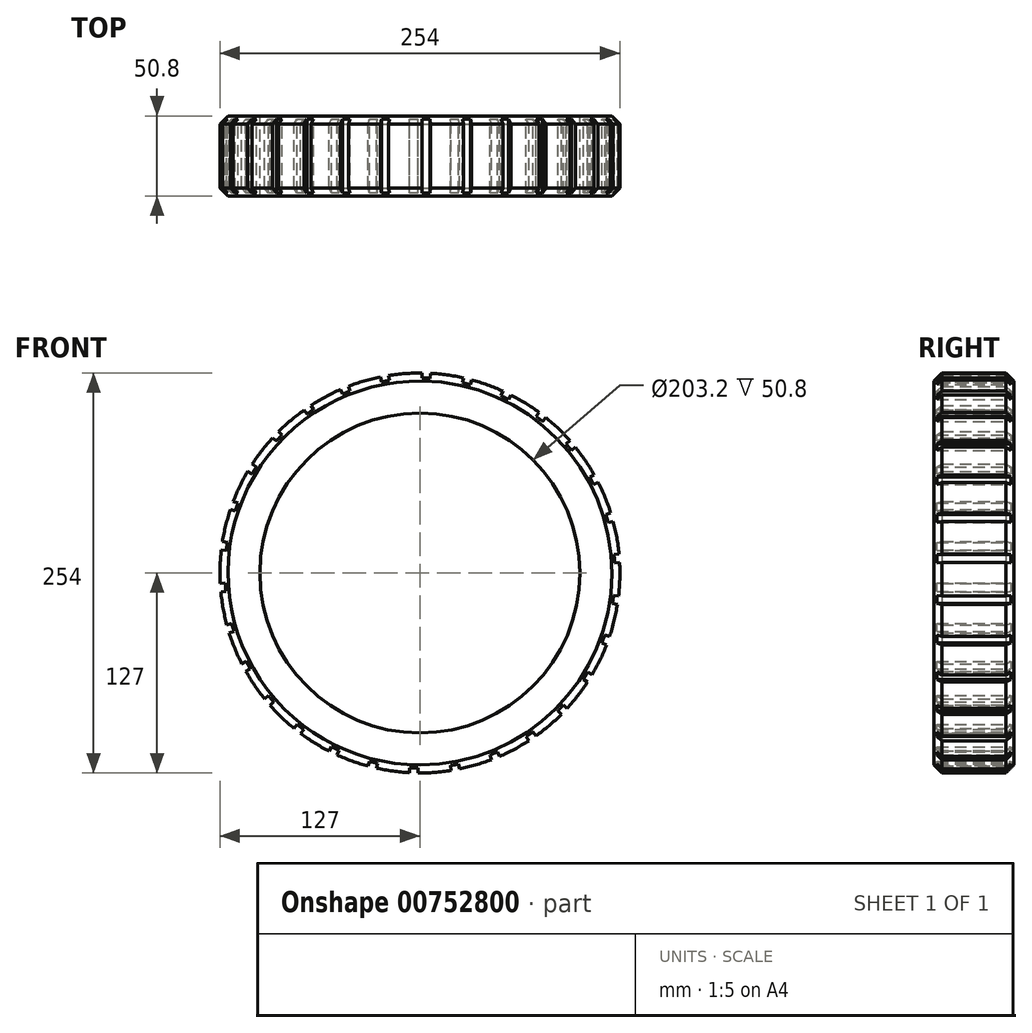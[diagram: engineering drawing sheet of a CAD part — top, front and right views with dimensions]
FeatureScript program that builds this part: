
annotation { "Feature Type Name" : "Feature", "Feature Type Description" : "" }
export const myFeature = defineFeature(function(context is Context, id is Id, definition is map)
    precondition{}
    {
        {
            var Q0;
            Q0=qCreatedBy(makeId("Front.planeOp"),FACE);
            var sketch = newSketch(context, id + "F0", { "sketchPlane" : qUnion([Q0])});
            skCircle(sketch, "E0", {"center": v(0, 0) * mm, "radius": 101.6 * mm});
            skCircle(sketch, "E1", {"center": v(0, 0) * mm, "radius": 127 * mm});
            skSolve(sketch);
        }
        {
            var Q0;
            Q0=makeQuery(id+"F0.imprint","IMPRINT",FACE,{"disambiguationData":[TD([[makeQuery(id+"F0.imprint","IMPRINT",EDGE,{"derivedFrom":sQuery(id+"F0.wireOp",EDGE,"E0")}),-1.0]])]});
            extrude(context, id + "F1", {"entities" : qUnion([Q0]), "depth" : 50.8 * mm, "offsetDistance" : 25.4 * mm});
        }
        {
            var Q0;
            Q0=makeQuery(id+"F1.opExtrude","CAP_EDGE",EDGE,{"disambiguationData":[OSD([sQuery(id+"F0.wireOp",EDGE,"E1")])],"isStart":true});
            var Q1;
            Q1=makeQuery(id+"F1.opExtrude","CAP_EDGE",EDGE,{"disambiguationData":[OSD([sQuery(id+"F0.wireOp",EDGE,"E1")])],"isStart":false});
            chamfer(context, id + "F2", {"entities" : qUnion([Q0, Q1]), "width" : 5.08 * mm, "tangentPropagation" : true});
        }
        {
            var Q0;
            Q0=qCreatedBy(makeId("Front.planeOp"),FACE);
            var sketch = newSketch(context, id + "F3", { "sketchPlane" : qUnion([Q0])});
            skArc(sketch, "E2", {"start": v(57.69, 113.14) * mm, "mid": v(55.26, 114.35) * mm, "end": v(52.8, 115.5) * mm});
            skArc(sketch, "E3", {"start": v(56.25, 110.31) * mm, "mid": v(53.88, 111.49) * mm, "end": v(51.48, 112.62) * mm});
            skLineSegment(sketch, "E4", {"start": v(51.48, 112.62) * mm, "end": v(52.8, 115.5) * mm});
            skLineSegment(sketch, "E5", {"start": v(56.25, 110.31) * mm, "end": v(57.69, 113.14) * mm});
            skLineSegment(sketch, "E6.1.0", {"start": v(26.94, 120.86) * mm, "end": v(27.63, 123.96) * mm});
            skArc(sketch, "E6.1.1", {"start": v(32.9, 122.66) * mm, "mid": v(30.28, 123.34) * mm, "end": v(27.63, 123.96) * mm});
            skArc(sketch, "E6.1.2", {"start": v(32.08, 119.6) * mm, "mid": v(29.52, 120.25) * mm, "end": v(26.94, 120.86) * mm});
            skLineSegment(sketch, "E6.1.3", {"start": v(32.08, 119.6) * mm, "end": v(32.9, 122.66) * mm});
            skLineSegment(sketch, "E6.2.0", {"start": v(1.23, 123.82) * mm, "end": v(1.26, 127) * mm});
            skArc(sketch, "E6.2.1", {"start": v(6.68, 126.82) * mm, "mid": v(3.97, 126.94) * mm, "end": v(1.26, 127) * mm});
            skArc(sketch, "E6.2.2", {"start": v(6.52, 123.65) * mm, "mid": v(3.87, 123.76) * mm, "end": v(1.23, 123.82) * mm});
            skLineSegment(sketch, "E6.2.3", {"start": v(6.52, 123.65) * mm, "end": v(6.68, 126.82) * mm});
            skLineSegment(sketch, "E6.3.0", {"start": v(-24.54, 121.37) * mm, "end": v(-25.17, 124.48) * mm});
            skArc(sketch, "E6.3.1", {"start": v(-19.83, 125.44) * mm, "mid": v(-22.5, 124.99) * mm, "end": v(-25.17, 124.48) * mm});
            skArc(sketch, "E6.3.2", {"start": v(-19.34, 122.3) * mm, "mid": v(-21.95, 121.86) * mm, "end": v(-24.54, 121.37) * mm});
            skLineSegment(sketch, "E6.3.3", {"start": v(-19.34, 122.3) * mm, "end": v(-19.83, 125.44) * mm});
            skLineSegment(sketch, "E6.4.0", {"start": v(-49.24, 113.61) * mm, "end": v(-50.5, 116.53) * mm});
            skArc(sketch, "E6.4.1", {"start": v(-45.48, 118.58) * mm, "mid": v(-48, 117.58) * mm, "end": v(-50.5, 116.53) * mm});
            skArc(sketch, "E6.4.2", {"start": v(-44.34, 115.61) * mm, "mid": v(-46.8, 114.64) * mm, "end": v(-49.24, 113.61) * mm});
            skLineSegment(sketch, "E6.4.3", {"start": v(-44.34, 115.61) * mm, "end": v(-45.48, 118.58) * mm});
            skLineSegment(sketch, "E6.5.0", {"start": v(-71.79, 100.9) * mm, "end": v(-73.63, 103.48) * mm});
            skArc(sketch, "E6.5.1", {"start": v(-69.14, 106.53) * mm, "mid": v(-71.4, 105.03) * mm, "end": v(-73.63, 103.48) * mm});
            skArc(sketch, "E6.5.2", {"start": v(-67.41, 103.87) * mm, "mid": v(-69.61, 102.4) * mm, "end": v(-71.79, 100.9) * mm});
            skLineSegment(sketch, "E6.5.3", {"start": v(-67.41, 103.87) * mm, "end": v(-69.14, 106.53) * mm});
            skLineSegment(sketch, "E6.6.0", {"start": v(-91.2, 83.76) * mm, "end": v(-93.53, 85.9) * mm});
            skArc(sketch, "E6.6.1", {"start": v(-89.78, 89.83) * mm, "mid": v(-91.68, 87.89) * mm, "end": v(-93.53, 85.9) * mm});
            skArc(sketch, "E6.6.2", {"start": v(-87.53, 87.58) * mm, "mid": v(-89.38, 85.7) * mm, "end": v(-91.2, 83.76) * mm});
            skLineSegment(sketch, "E6.6.3", {"start": v(-87.53, 87.58) * mm, "end": v(-89.78, 89.83) * mm});
            skLineSegment(sketch, "E6.7.0", {"start": v(-106.62, 62.97) * mm, "end": v(-109.35, 64.59) * mm});
            skArc(sketch, "E6.7.1", {"start": v(-106.5, 69.2) * mm, "mid": v(-107.95, 66.9) * mm, "end": v(-109.35, 64.59) * mm});
            skArc(sketch, "E6.7.2", {"start": v(-103.83, 67.47) * mm, "mid": v(-105.25, 65.24) * mm, "end": v(-106.62, 62.97) * mm});
            skLineSegment(sketch, "E6.7.3", {"start": v(-103.83, 67.47) * mm, "end": v(-106.5, 69.2) * mm});
            skLineSegment(sketch, "E6.8.0", {"start": v(-117.38, 39.43) * mm, "end": v(-120.39, 40.44) * mm});
            skArc(sketch, "E6.8.1", {"start": v(-118.55, 45.55) * mm, "mid": v(-119.5, 43) * mm, "end": v(-120.39, 40.44) * mm});
            skArc(sketch, "E6.8.2", {"start": v(-115.59, 44.4) * mm, "mid": v(-116.51, 41.93) * mm, "end": v(-117.38, 39.43) * mm});
            skLineSegment(sketch, "E6.8.3", {"start": v(-115.59, 44.4) * mm, "end": v(-118.55, 45.55) * mm});
            skLineSegment(sketch, "E6.9.0", {"start": v(-123.01, 14.16) * mm, "end": v(-126.17, 14.53) * mm});
            skArc(sketch, "E6.9.1", {"start": v(-125.43, 19.9) * mm, "mid": v(-125.83, 17.22) * mm, "end": v(-126.17, 14.53) * mm});
            skArc(sketch, "E6.9.2", {"start": v(-122.3, 19.4) * mm, "mid": v(-122.68, 16.79) * mm, "end": v(-123.01, 14.16) * mm});
            skLineSegment(sketch, "E6.9.3", {"start": v(-122.3, 19.4) * mm, "end": v(-125.43, 19.9) * mm});
            skLineSegment(sketch, "E6.10.0", {"start": v(-123.27, -11.72) * mm, "end": v(-126.43, -12.02) * mm});
            skArc(sketch, "E6.10.1", {"start": v(-126.83, -6.61) * mm, "mid": v(-126.66, -9.32) * mm, "end": v(-126.43, -12.02) * mm});
            skArc(sketch, "E6.10.2", {"start": v(-123.66, -6.45) * mm, "mid": v(-123.5, -9.09) * mm, "end": v(-123.27, -11.72) * mm});
            skLineSegment(sketch, "E6.10.3", {"start": v(-123.66, -6.45) * mm, "end": v(-126.83, -6.61) * mm});
            skLineSegment(sketch, "E6.11.0", {"start": v(-118.14, -37.1) * mm, "end": v(-121.17, -38.05) * mm});
            skArc(sketch, "E6.11.1", {"start": v(-122.68, -32.84) * mm, "mid": v(-121.95, -35.45) * mm, "end": v(-121.17, -38.05) * mm});
            skArc(sketch, "E6.11.2", {"start": v(-119.61, -32.01) * mm, "mid": v(-118.9, -34.56) * mm, "end": v(-118.14, -37.1) * mm});
            skLineSegment(sketch, "E6.11.3", {"start": v(-119.61, -32.01) * mm, "end": v(-122.68, -32.84) * mm});
            skLineSegment(sketch, "E6.12.0", {"start": v(-107.84, -60.85) * mm, "end": v(-110.6, -62.4) * mm});
            skArc(sketch, "E6.12.1", {"start": v(-113.17, -57.62) * mm, "mid": v(-111.92, -60.03) * mm, "end": v(-110.6, -62.4) * mm});
            skArc(sketch, "E6.12.2", {"start": v(-110.34, -56.18) * mm, "mid": v(-109.12, -58.53) * mm, "end": v(-107.84, -60.85) * mm});
            skLineSegment(sketch, "E6.12.3", {"start": v(-110.34, -56.18) * mm, "end": v(-113.17, -57.62) * mm});
            skLineSegment(sketch, "E6.13.0", {"start": v(-92.84, -81.94) * mm, "end": v(-95.22, -84.04) * mm});
            skArc(sketch, "E6.13.1", {"start": v(-98.72, -79.9) * mm, "mid": v(-97, -81.99) * mm, "end": v(-95.22, -84.04) * mm});
            skArc(sketch, "E6.13.2", {"start": v(-96.25, -77.9) * mm, "mid": v(-94.57, -79.94) * mm, "end": v(-92.84, -81.94) * mm});
            skLineSegment(sketch, "E6.13.3", {"start": v(-96.25, -77.9) * mm, "end": v(-98.72, -79.9) * mm});
            skLineSegment(sketch, "E6.14.0", {"start": v(-73.77, -99.45) * mm, "end": v(-75.66, -102) * mm});
            skArc(sketch, "E6.14.1", {"start": v(-79.95, -98.68) * mm, "mid": v(-77.82, -100.36) * mm, "end": v(-75.66, -102) * mm});
            skArc(sketch, "E6.14.2", {"start": v(-77.95, -96.2) * mm, "mid": v(-75.88, -97.85) * mm, "end": v(-73.77, -99.45) * mm});
            skLineSegment(sketch, "E6.14.3", {"start": v(-77.95, -96.2) * mm, "end": v(-79.95, -98.68) * mm});
            skLineSegment(sketch, "E6.15.0", {"start": v(-51.48, -112.62) * mm, "end": v(-52.8, -115.5) * mm});
            skArc(sketch, "E6.15.1", {"start": v(-57.69, -113.14) * mm, "mid": v(-55.26, -114.35) * mm, "end": v(-52.8, -115.5) * mm});
            skArc(sketch, "E6.15.2", {"start": v(-56.25, -110.31) * mm, "mid": v(-53.88, -111.49) * mm, "end": v(-51.48, -112.62) * mm});
            skLineSegment(sketch, "E6.15.3", {"start": v(-56.25, -110.31) * mm, "end": v(-57.69, -113.14) * mm});
            skLineSegment(sketch, "E6.16.0", {"start": v(-26.94, -120.86) * mm, "end": v(-27.63, -123.96) * mm});
            skArc(sketch, "E6.16.1", {"start": v(-32.9, -122.66) * mm, "mid": v(-30.28, -123.34) * mm, "end": v(-27.63, -123.96) * mm});
            skArc(sketch, "E6.16.2", {"start": v(-32.08, -119.6) * mm, "mid": v(-29.52, -120.25) * mm, "end": v(-26.94, -120.86) * mm});
            skLineSegment(sketch, "E6.16.3", {"start": v(-32.08, -119.6) * mm, "end": v(-32.9, -122.66) * mm});
            skLineSegment(sketch, "E6.17.0", {"start": v(-1.23, -123.82) * mm, "end": v(-1.26, -127) * mm});
            skArc(sketch, "E6.17.1", {"start": v(-6.68, -126.82) * mm, "mid": v(-3.97, -126.94) * mm, "end": v(-1.26, -127) * mm});
            skArc(sketch, "E6.17.2", {"start": v(-6.52, -123.65) * mm, "mid": v(-3.87, -123.76) * mm, "end": v(-1.23, -123.82) * mm});
            skLineSegment(sketch, "E6.17.3", {"start": v(-6.52, -123.65) * mm, "end": v(-6.68, -126.82) * mm});
            skLineSegment(sketch, "E6.18.0", {"start": v(24.54, -121.37) * mm, "end": v(25.17, -124.48) * mm});
            skArc(sketch, "E6.18.1", {"start": v(19.83, -125.44) * mm, "mid": v(22.5, -124.99) * mm, "end": v(25.17, -124.48) * mm});
            skArc(sketch, "E6.18.2", {"start": v(19.34, -122.3) * mm, "mid": v(21.95, -121.86) * mm, "end": v(24.54, -121.37) * mm});
            skLineSegment(sketch, "E6.18.3", {"start": v(19.34, -122.3) * mm, "end": v(19.83, -125.44) * mm});
            skLineSegment(sketch, "E6.19.0", {"start": v(49.24, -113.61) * mm, "end": v(50.5, -116.53) * mm});
            skArc(sketch, "E6.19.1", {"start": v(45.48, -118.58) * mm, "mid": v(48, -117.58) * mm, "end": v(50.5, -116.53) * mm});
            skArc(sketch, "E6.19.2", {"start": v(44.34, -115.61) * mm, "mid": v(46.8, -114.64) * mm, "end": v(49.24, -113.61) * mm});
            skLineSegment(sketch, "E6.19.3", {"start": v(44.34, -115.61) * mm, "end": v(45.48, -118.58) * mm});
            skLineSegment(sketch, "E6.20.0", {"start": v(71.79, -100.9) * mm, "end": v(73.63, -103.48) * mm});
            skArc(sketch, "E6.20.1", {"start": v(69.14, -106.53) * mm, "mid": v(71.4, -105.03) * mm, "end": v(73.63, -103.48) * mm});
            skArc(sketch, "E6.20.2", {"start": v(67.41, -103.87) * mm, "mid": v(69.61, -102.4) * mm, "end": v(71.79, -100.9) * mm});
            skLineSegment(sketch, "E6.20.3", {"start": v(67.41, -103.87) * mm, "end": v(69.14, -106.53) * mm});
            skLineSegment(sketch, "E6.21.0", {"start": v(91.2, -83.76) * mm, "end": v(93.53, -85.9) * mm});
            skArc(sketch, "E6.21.1", {"start": v(89.78, -89.83) * mm, "mid": v(91.68, -87.89) * mm, "end": v(93.53, -85.9) * mm});
            skArc(sketch, "E6.21.2", {"start": v(87.53, -87.58) * mm, "mid": v(89.38, -85.7) * mm, "end": v(91.2, -83.76) * mm});
            skLineSegment(sketch, "E6.21.3", {"start": v(87.53, -87.58) * mm, "end": v(89.78, -89.83) * mm});
            skLineSegment(sketch, "E6.22.0", {"start": v(106.62, -62.97) * mm, "end": v(109.35, -64.59) * mm});
            skArc(sketch, "E6.22.1", {"start": v(106.5, -69.2) * mm, "mid": v(107.95, -66.9) * mm, "end": v(109.35, -64.59) * mm});
            skArc(sketch, "E6.22.2", {"start": v(103.83, -67.47) * mm, "mid": v(105.25, -65.24) * mm, "end": v(106.62, -62.97) * mm});
            skLineSegment(sketch, "E6.22.3", {"start": v(103.83, -67.47) * mm, "end": v(106.5, -69.2) * mm});
            skLineSegment(sketch, "E6.23.0", {"start": v(117.38, -39.43) * mm, "end": v(120.39, -40.44) * mm});
            skArc(sketch, "E6.23.1", {"start": v(118.55, -45.55) * mm, "mid": v(119.5, -43) * mm, "end": v(120.39, -40.44) * mm});
            skArc(sketch, "E6.23.2", {"start": v(115.59, -44.4) * mm, "mid": v(116.51, -41.93) * mm, "end": v(117.38, -39.43) * mm});
            skLineSegment(sketch, "E6.23.3", {"start": v(115.59, -44.4) * mm, "end": v(118.55, -45.55) * mm});
            skLineSegment(sketch, "E6.24.0", {"start": v(123.01, -14.16) * mm, "end": v(126.17, -14.53) * mm});
            skArc(sketch, "E6.24.1", {"start": v(125.43, -19.9) * mm, "mid": v(125.83, -17.22) * mm, "end": v(126.17, -14.53) * mm});
            skArc(sketch, "E6.24.2", {"start": v(122.3, -19.4) * mm, "mid": v(122.68, -16.79) * mm, "end": v(123.01, -14.16) * mm});
            skLineSegment(sketch, "E6.24.3", {"start": v(122.3, -19.4) * mm, "end": v(125.43, -19.9) * mm});
            skLineSegment(sketch, "E6.25.0", {"start": v(123.27, 11.72) * mm, "end": v(126.43, 12.02) * mm});
            skArc(sketch, "E6.25.1", {"start": v(126.83, 6.61) * mm, "mid": v(126.66, 9.32) * mm, "end": v(126.43, 12.02) * mm});
            skArc(sketch, "E6.25.2", {"start": v(123.66, 6.45) * mm, "mid": v(123.5, 9.09) * mm, "end": v(123.27, 11.72) * mm});
            skLineSegment(sketch, "E6.25.3", {"start": v(123.66, 6.45) * mm, "end": v(126.83, 6.61) * mm});
            skLineSegment(sketch, "E6.26.0", {"start": v(118.14, 37.1) * mm, "end": v(121.17, 38.05) * mm});
            skArc(sketch, "E6.26.1", {"start": v(122.68, 32.84) * mm, "mid": v(121.95, 35.45) * mm, "end": v(121.17, 38.05) * mm});
            skArc(sketch, "E6.26.2", {"start": v(119.61, 32.01) * mm, "mid": v(118.9, 34.56) * mm, "end": v(118.14, 37.1) * mm});
            skLineSegment(sketch, "E6.26.3", {"start": v(119.61, 32.01) * mm, "end": v(122.68, 32.84) * mm});
            skLineSegment(sketch, "E6.27.0", {"start": v(107.84, 60.85) * mm, "end": v(110.6, 62.4) * mm});
            skArc(sketch, "E6.27.1", {"start": v(113.17, 57.62) * mm, "mid": v(111.92, 60.03) * mm, "end": v(110.6, 62.4) * mm});
            skArc(sketch, "E6.27.2", {"start": v(110.34, 56.18) * mm, "mid": v(109.12, 58.53) * mm, "end": v(107.84, 60.85) * mm});
            skLineSegment(sketch, "E6.27.3", {"start": v(110.34, 56.18) * mm, "end": v(113.17, 57.62) * mm});
            skLineSegment(sketch, "E6.28.0", {"start": v(92.84, 81.94) * mm, "end": v(95.22, 84.04) * mm});
            skArc(sketch, "E6.28.1", {"start": v(98.72, 79.9) * mm, "mid": v(97, 81.99) * mm, "end": v(95.22, 84.04) * mm});
            skArc(sketch, "E6.28.2", {"start": v(96.25, 77.9) * mm, "mid": v(94.57, 79.94) * mm, "end": v(92.84, 81.94) * mm});
            skLineSegment(sketch, "E6.28.3", {"start": v(96.25, 77.9) * mm, "end": v(98.72, 79.9) * mm});
            skLineSegment(sketch, "E6.29.0", {"start": v(73.77, 99.45) * mm, "end": v(75.66, 102) * mm});
            skArc(sketch, "E6.29.1", {"start": v(79.95, 98.68) * mm, "mid": v(77.82, 100.36) * mm, "end": v(75.66, 102) * mm});
            skArc(sketch, "E6.29.2", {"start": v(77.95, 96.2) * mm, "mid": v(75.88, 97.85) * mm, "end": v(73.77, 99.45) * mm});
            skLineSegment(sketch, "E6.29.3", {"start": v(77.95, 96.2) * mm, "end": v(79.95, 98.68) * mm});
            skSolve(sketch);
        }
        {
            var Q0;
            Q0 = qSketchRegion(id + "F3", true);
            extrude(context, id + "F4", {"entities" : qUnion([Q0]), "operationType" : NewBodyOperationType.REMOVE, "depth" : 50.8 * mm, "offsetDistance" : 25.4 * mm});
        }
    });
